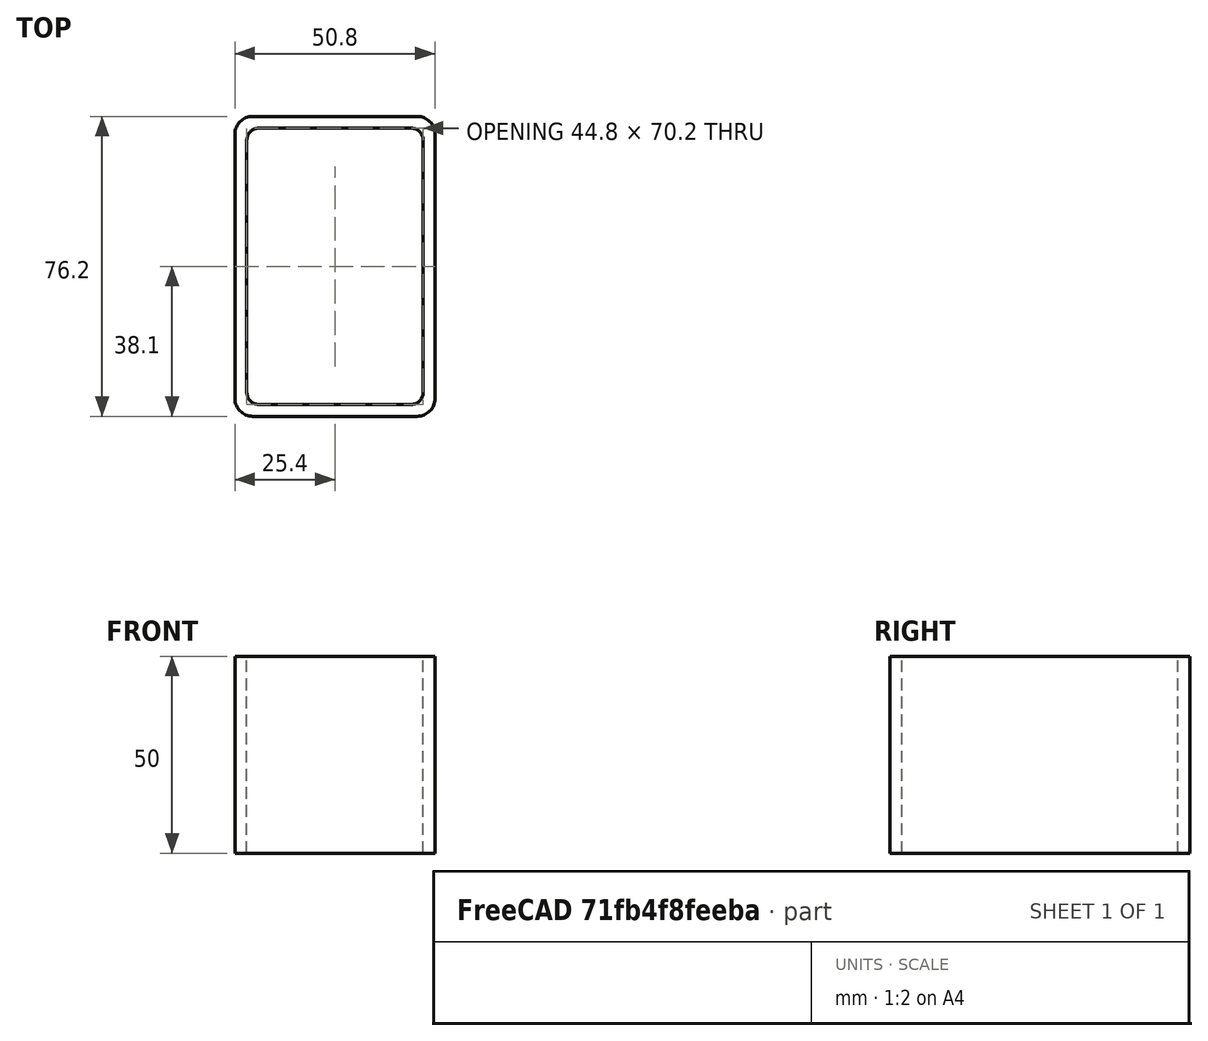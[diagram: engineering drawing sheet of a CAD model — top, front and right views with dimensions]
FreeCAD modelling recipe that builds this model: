
FCSTD DOCUMENT  (FreeCAD 0.15R4671 (Git))
Label: Rectangular hollow section 76.2 x50.8 x3 EN10219 S235JRH
License: All rights reserved
LicenseURL: http://en.wikipedia.org/wiki/All_rights_reserved
objects: Sketcher::SketchObject×1, Part::Extrusion×1
note: 2 computed .brp shape members not serialized (recipe doc carries the construction recipe); baked Part::Feature solids carry a one-line shape summary decoded from their .brp

FEATURE [Sketcher::SketchObject] Sketch
  sketch-geometry (16):
    g0: LineSegment StartX=-19.4 StartY=35.1 StartZ=0 EndX=19.4 EndY=35.1 EndZ=0
    g1: LineSegment StartX=22.4 StartY=32.1 StartZ=0 EndX=22.4 EndY=-32.1 EndZ=0
    g2: LineSegment StartX=19.4 StartY=-35.1 StartZ=0 EndX=-19.4 EndY=-35.1 EndZ=0
    g3: LineSegment StartX=-22.4 StartY=-32.1 StartZ=0 EndX=-22.4 EndY=32.1 EndZ=0
    g4: LineSegment StartX=-20.9 StartY=38.1 StartZ=0 EndX=20.9 EndY=38.1 EndZ=0
    g5: LineSegment StartX=25.4 StartY=33.6 StartZ=0 EndX=25.4 EndY=-33.6 EndZ=0
    g6: LineSegment StartX=20.9 StartY=-38.1 StartZ=0 EndX=-20.9 EndY=-38.1 EndZ=0
    g7: LineSegment StartX=-25.4 StartY=-33.6 StartZ=0 EndX=-25.4 EndY=33.6 EndZ=0
    g8: ArcOfCircle CenterX=-19.4 CenterY=32.1 CenterZ=0 NormalX=0 NormalY=0 NormalZ=1 Radius=3 StartAngle=1.5708 EndAngle=3.14159
    g9: ArcOfCircle CenterX=19.4 CenterY=32.1 CenterZ=0 NormalX=0 NormalY=0 NormalZ=1 Radius=3 StartAngle=0 EndAngle=1.5708
    g10: ArcOfCircle CenterX=19.4 CenterY=-32.1 CenterZ=0 NormalX=0 NormalY=0 NormalZ=1 Radius=3 StartAngle=4.71239 EndAngle=6.28319
    g11: ArcOfCircle CenterX=-19.4 CenterY=-32.1 CenterZ=0 NormalX=0 NormalY=0 NormalZ=1 Radius=3 StartAngle=3.14159 EndAngle=4.71239
    g12: ArcOfCircle CenterX=20.9 CenterY=33.6 CenterZ=0 NormalX=0 NormalY=0 NormalZ=1 Radius=4.5 StartAngle=0 EndAngle=1.5708
    g13: ArcOfCircle CenterX=20.9 CenterY=-33.6 CenterZ=0 NormalX=0 NormalY=0 NormalZ=1 Radius=4.5 StartAngle=4.71239 EndAngle=6.28319
    g14: ArcOfCircle CenterX=-20.9 CenterY=-33.6 CenterZ=0 NormalX=0 NormalY=0 NormalZ=1 Radius=4.5 StartAngle=3.14159 EndAngle=4.71239
    g15: ArcOfCircle CenterX=-20.9 CenterY=33.6 CenterZ=0 NormalX=0 NormalY=0 NormalZ=1 Radius=4.5 StartAngle=1.5708 EndAngle=3.14159
  constraints (36):
    c: Horizontal(g2)
    c: Vertical(g3)
    c: Horizontal(g6)
    c: Vertical(g7)
    c: Tangent(g3,g8) = 1.5708
    c: Tangent(g0,g8) = 1.5708
    c: Tangent(g0,g9) = 1.5708
    c: Tangent(g1,g9) = 1.5708
    c: Tangent(g1,g10) = 1.5708
    c: Tangent(g2,g10) = 1.5708
    c: Tangent(g2,g11) = 1.5708
    c: Tangent(g3,g11) = 1.5708
    c: Tangent(g4,g12) = 1.5708
    c: Tangent(g5,g12) = 1.5708
    c: Tangent(g5,g13) = 1.5708
    c: Tangent(g6,g13) = 1.5708
    c: Tangent(g6,g14) = 1.5708
    c: Tangent(g7,g14) = 1.5708
    c: Tangent(g7,g15) = 1.5708
    c: Tangent(g4,g15) = 1.5708
    c: Equal(g9,g8)
    c: Equal(g9,g11)
    c: Equal(g9,g10)
    c: Equal(g12,g15)
    c: Equal(g12,g14)
    c: Equal(g12,g13)
    c: Symmetric(g4,g6,g-1)
    c: Symmetric(g7,g5,g-2)
    c: DistanceY(g4,g6) = -76.2
    c: DistanceX(g7,g5) = 50.8
    c: Symmetric(g3,g1,g-2)
    c: Symmetric(g0,g2,g-1)
    c: DistanceY(g0,g4) = 3
    c: DistanceX(g5,g1) = -3
    c: Radius(g9) = 3
    c: Radius(g12) = 4.5
FEATURE [Part::Extrusion] Extrude  label="Rectangular hollow section 76.2 x50.8 x3 EN10219 S235JRH"
  Base = -> Sketch
  Dir = (0,0,50)
  Solid = true
